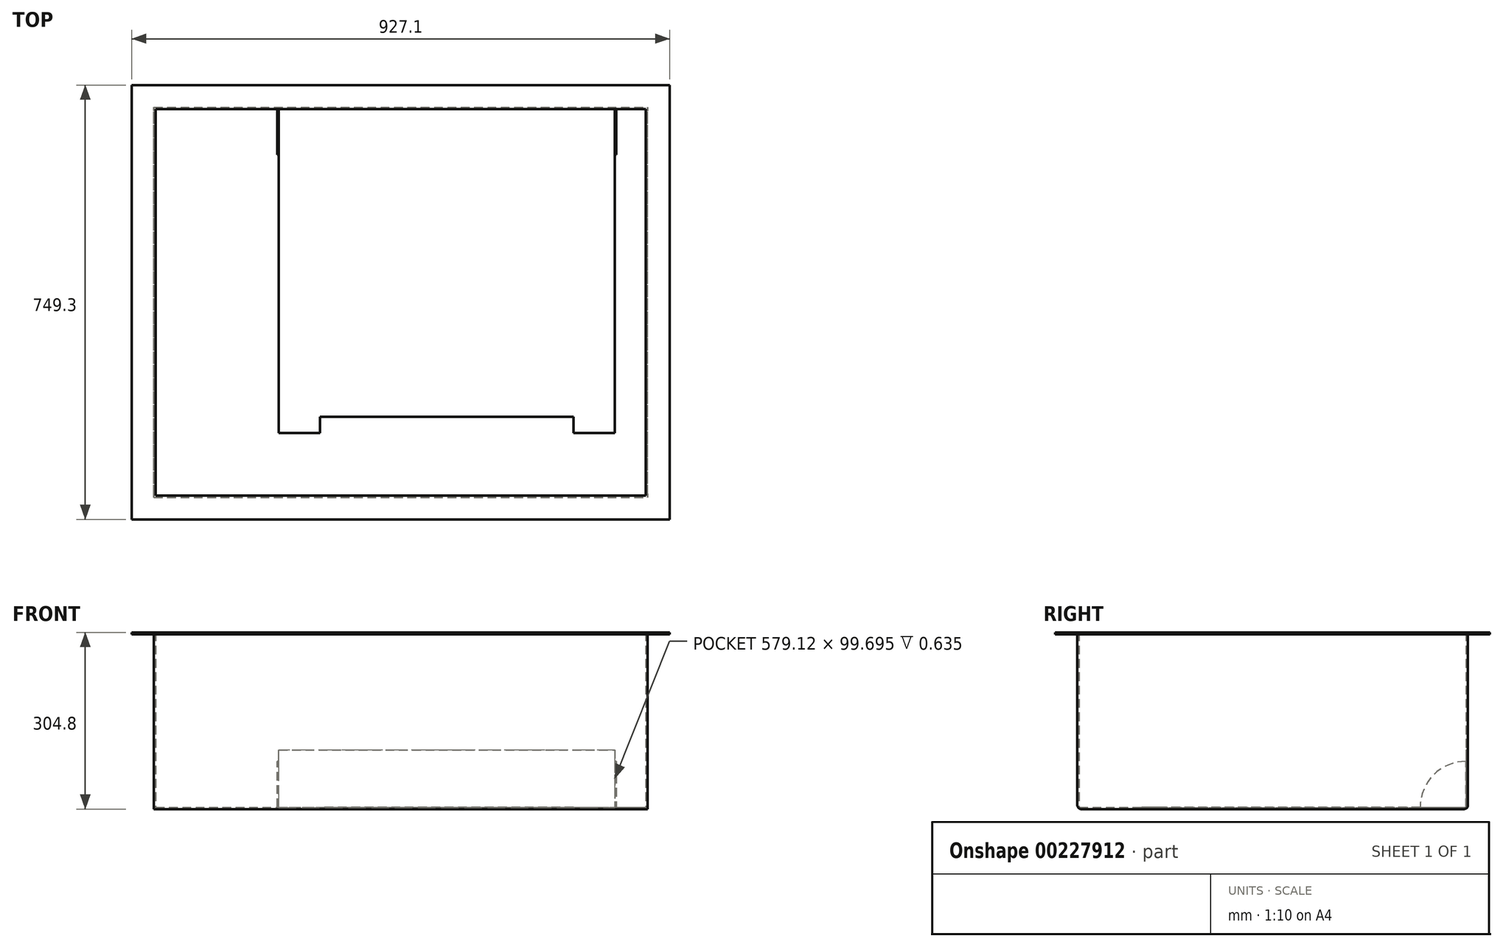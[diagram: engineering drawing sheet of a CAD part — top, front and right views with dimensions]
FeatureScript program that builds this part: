
annotation { "Feature Type Name" : "Feature", "Feature Type Description" : "" }
export const myFeature = defineFeature(function(context is Context, id is Id, definition is map)
    precondition{}
    {
        {
            var Q0;
            Q0=qCreatedBy(makeId("Top.planeOp"),FACE);
            var sketch = newSketch(context, id + "F0", { "sketchPlane" : qUnion([Q0])});
            skLineSegment(sketch, "E0.bottom", {"start": v(-425.45, -336.55) * mm, "end": v(425.45, -336.55) * mm});
            skLineSegment(sketch, "E0.top", {"start": v(-425.45, 336.55) * mm, "end": v(425.45, 336.55) * mm});
            skLineSegment(sketch, "E0.left", {"start": v(-425.45, -336.55) * mm, "end": v(-425.45, 336.55) * mm});
            skLineSegment(sketch, "E0.right", {"start": v(425.45, -336.55) * mm, "end": v(425.45, 336.55) * mm});
            skPoint(sketch, "E0.middle", {"position": v(0, 0) * mm});
            skSolve(sketch);
        }
        {
            var Q0;
            Q0=makeQuery(id+"F0.imprint","IMPRINT",FACE,{"disambiguationData":[TD([[makeQuery(id+"F0.imprint","IMPRINT",EDGE,{"derivedFrom":sQuery(id+"F0.wireOp",EDGE,"E0.bottom")}),1.0]])]});
            extrude(context, id + "F1", {"entities" : qUnion([Q0]), "depth" : 304.8 * mm});
        }
        {
            var Q0;
            Q0=makeQuery(id+"F1.opExtrude","CAP_FACE",FACE,{"disambiguationData":[OSD([sQuery(id+"F0.wireOp",EDGE,"E0.bottom"),sQuery(id+"F0.wireOp",EDGE,"E0.top"),sQuery(id+"F0.wireOp",EDGE,"E0.left"),sQuery(id+"F0.wireOp",EDGE,"E0.right")])],"isStart":false});
            shell(context, id + "F2", {"entities" : qUnion([Q0]), "thickness" : 3.17 * mm});
        }
        {
            var Q0;
            Q0=makeQuery(id+"F2.opShell","OFFSET_FACE",FACE,{"disambiguationData":[OSD([sQuery(id+"F0.wireOp",EDGE,"E0.top")])]});
            var sketch = newSketch(context, id + "F3", { "sketchPlane" : qUnion([Q0])});
            skLineSegment(sketch, "E1.0", {"start": v(371.48, 304.8) * mm, "end": v(371.48, 3.17) * mm});
            skLineSegment(sketch, "E2", {"start": v(371.48, 3.17) * mm, "end": v(-212.72, 3.17) * mm});
            skLineSegment(sketch, "E3", {"start": v(-212.72, 3.17) * mm, "end": v(-212.72, 104.78) * mm});
            skLineSegment(sketch, "E4", {"start": v(-212.72, 104.78) * mm, "end": v(371.48, 104.78) * mm});
            skSolve(sketch);
        }
        {
            var Q0;
            {var subQ0=sQuery(id+"F3.wireOp",EDGE,"E2");Q0=makeQuery(id+"F3.imprint","IMPRINT",FACE,{"disambiguationData":[TD([[makeQuery(id+"F3.imprint","IMPRINT",EDGE,{"derivedFrom":subQ0}),1.0]])]});}
            extrude(context, id + "F4", {"entities" : qUnion([Q0]), "operationType" : NewBodyOperationType.ADD, "depth" : 558.8 * mm});
        }
        {
            var Q0;
            Q0=makeQuery(id+"F4.opExtrude","CAP_FACE",FACE,{"disambiguationData":[OSD([sQuery(id+"F3.wireOp",EDGE,"E1.0"),sQuery(id+"F3.wireOp",EDGE,"E2"),sQuery(id+"F3.wireOp",EDGE,"E3"),sQuery(id+"F3.wireOp",EDGE,"E4")])],"isStart":false});
            var sketch = newSketch(context, id + "F5", { "sketchPlane" : qUnion([Q0])});
            skLineSegment(sketch, "E5.0", {"start": v(-136.52, 3.17) * mm, "end": v(-136.52, 104.78) * mm});
            skLineSegment(sketch, "E6.0", {"start": v(295.28, 104.78) * mm, "end": v(295.28, 3.17) * mm});
            skLineSegment(sketch, "E7.0", {"start": v(-212.72, 73.03) * mm, "end": v(371.48, 73.03) * mm});
            skSolve(sketch);
        }
        {
            var Q0;
            {var subQ0=sQuery(id+"F5.wireOp",EDGE,"E5.0");var subQ1=makeQuery(id+"F4.opExtrude","CAP_EDGE",EDGE,{"disambiguationData":[OSD([sQuery(id+"F3.wireOp",EDGE,"E2")])],"isStart":false});var subQ2=makeQuery(id+"F5.imprint","INTERSECT",VERTEX,{"derivedFrom":[subQ1,subQ0]});Q0=makeQuery(id+"F5.imprint","IMPRINT",FACE,{"disambiguationData":[TD([[makeQuery(id+"F5.imprint","IMPRINT",EDGE,{"disambiguationData":[TD([[subQ2,-1.0]])],"derivedFrom":subQ0}),-1.0]])]});}
            extrude(context, id + "F6", {"entities" : qUnion([Q0]), "operationType" : NewBodyOperationType.REMOVE, "oppositeDirection" : true, "depth" : 25.4 * mm});
        }
        {
            var Q0;
            Q0=makeQuery(id+"F4.opExtrude","CAP_FACE",FACE,{"disambiguationData":[OSD([sQuery(id+"F3.wireOp",EDGE,"E1.0"),sQuery(id+"F3.wireOp",EDGE,"E2"),sQuery(id+"F3.wireOp",EDGE,"E3"),sQuery(id+"F3.wireOp",EDGE,"E4")])],"isStart":false});
            shell(context, id + "F7", {"entities" : qUnion([Q0]), "thickness" : 2.54 * mm});
        }
        {
            var Q0;
            Q0=makeQuery(id+"F4.opExtrude","SWEPT_FACE",FACE,{"disambiguationData":[OSD([sQuery(id+"F3.wireOp",EDGE,"E4")])]});
            var sketch = newSketch(context, id + "F8", { "sketchPlane" : qUnion([Q0])});
            skLineSegment(sketch, "E8.0", {"start": v(-60.32, -225.43) * mm, "end": v(-60.32, 333.38) * mm, "construction": true});
            skLineSegment(sketch, "E9.0", {"start": v(219.08, -225.43) * mm, "end": v(219.08, 333.38) * mm, "construction": true});
            skLineSegment(sketch, "E10.0", {"start": v(-212.72, 269.88) * mm, "end": v(371.48, 269.88) * mm, "construction": true});
            skLineSegment(sketch, "E11.0", {"start": v(-212.72, -161.93) * mm, "end": v(371.48, -161.93) * mm, "construction": true});
            skCircle(sketch, "E12", {"center": v(-60.32, 269.88) * mm, "radius": 24.06 * mm, "construction": true});
            skCircle(sketch, "E13", {"center": v(219.08, 269.88) * mm, "radius": 28.85 * mm, "construction": true});
            skCircle(sketch, "E14", {"center": v(219.08, -161.93) * mm, "radius": 29.69 * mm, "construction": true});
            skCircle(sketch, "E15", {"center": v(-60.32, -161.93) * mm, "radius": 21.62 * mm, "construction": true});
            skCircle(sketch, "E16", {"center": v(-60.32, 269.88) * mm, "radius": 6.35 * mm});
            skCircle(sketch, "E17", {"center": v(219.08, 269.88) * mm, "radius": 6.35 * mm});
            skCircle(sketch, "E18", {"center": v(-60.32, -161.93) * mm, "radius": 6.35 * mm});
            skCircle(sketch, "E19", {"center": v(219.08, -161.93) * mm, "radius": 6.35 * mm});
            skSolve(sketch);
        }
        {
            var Q0;
            Q0=makeQuery(id+"F8.imprint","IMPRINT",FACE,{"disambiguationData":[TD([[makeQuery(id+"F8.imprint","IMPRINT",EDGE,{"derivedFrom":sQuery(id+"F8.wireOp",EDGE,"E17")}),1.0]])]});
            var Q1;
            Q1=makeQuery(id+"F8.imprint","IMPRINT",FACE,{"disambiguationData":[TD([[makeQuery(id+"F8.imprint","IMPRINT",EDGE,{"derivedFrom":sQuery(id+"F8.wireOp",EDGE,"E16")}),1.0]])]});
            var Q2;
            Q2=makeQuery(id+"F8.imprint","IMPRINT",FACE,{"disambiguationData":[TD([[makeQuery(id+"F8.imprint","IMPRINT",EDGE,{"derivedFrom":sQuery(id+"F8.wireOp",EDGE,"E18")}),1.0]])]});
            var Q3;
            Q3=makeQuery(id+"F8.imprint","IMPRINT",FACE,{"disambiguationData":[TD([[makeQuery(id+"F8.imprint","IMPRINT",EDGE,{"derivedFrom":sQuery(id+"F8.wireOp",EDGE,"E19")}),1.0]])]});
            extrude(context, id + "F9", {"entities" : qUnion([Q0, Q1, Q2, Q3]), "operationType" : NewBodyOperationType.REMOVE, "endBound" : BoundingType.UP_TO_NEXT, "oppositeDirection" : true, "depth" : 25.4 * mm});
        }
        {
            var Q0;
            Q0=makeQuery(id+"F1.opExtrude","CAP_FACE",FACE,{"disambiguationData":[OSD([sQuery(id+"F0.wireOp",EDGE,"E0.bottom"),sQuery(id+"F0.wireOp",EDGE,"E0.top"),sQuery(id+"F0.wireOp",EDGE,"E0.left"),sQuery(id+"F0.wireOp",EDGE,"E0.right")])],"isStart":false});
            var sketch = newSketch(context, id + "F10", { "sketchPlane" : qUnion([Q0])});
            skLineSegment(sketch, "E20.0", {"start": v(-463.55, 374.65) * mm, "end": v(463.55, 374.65) * mm});
            skLineSegment(sketch, "E21.0", {"start": v(-463.55, -374.65) * mm, "end": v(-463.55, 374.65) * mm});
            skLineSegment(sketch, "E22.0", {"start": v(463.55, -374.65) * mm, "end": v(463.55, 374.65) * mm});
            skLineSegment(sketch, "E23.0", {"start": v(-463.55, -374.65) * mm, "end": v(463.55, -374.65) * mm});
            skLineSegment(sketch, "E24.0", {"start": v(-425.45, -336.55) * mm, "end": v(-425.45, 336.55) * mm});
            skLineSegment(sketch, "E25.0", {"start": v(-425.45, -336.55) * mm, "end": v(425.45, -336.55) * mm});
            skLineSegment(sketch, "E26.0", {"start": v(-425.45, 336.55) * mm, "end": v(425.45, 336.55) * mm});
            skLineSegment(sketch, "E27.0", {"start": v(425.45, -336.55) * mm, "end": v(425.45, 336.55) * mm});
            skSolve(sketch);
        }
        {
            var Q0;
            Q0=makeQuery(id+"F10.imprint","IMPRINT",FACE,{"disambiguationData":[TD([[makeQuery(id+"F10.imprint","IMPRINT",EDGE,{"derivedFrom":sQuery(id+"F10.wireOp",EDGE,"E20.0")}),-1.0]])]});
            extrude(context, id + "F11", {"entities" : qUnion([Q0]), "operationType" : NewBodyOperationType.ADD, "oppositeDirection" : true, "depth" : 3.17 * mm});
        }
        {
            var Q0;
            Q0=makeQuery(id+"F1.opExtrude","CAP_EDGE",EDGE,{"disambiguationData":[OSD([sQuery(id+"F0.wireOp",EDGE,"E0.bottom")])],"isStart":true});
            fillet(context, id + "F12", {"entities" : qUnion([Q0]), "radius" : 6.35 * mm, "tangentPropagation" : true, "allowEdgeOverflow" : false});
        }
        {
            var Q0;
            Q0=makeQuery(id+"F1.opExtrude","CAP_EDGE",EDGE,{"disambiguationData":[OSD([sQuery(id+"F0.wireOp",EDGE,"E0.top")])],"isStart":true});
            fillet(context, id + "F13", {"entities" : qUnion([Q0]), "radius" : 6.35 * mm, "tangentPropagation" : true, "allowEdgeOverflow" : false});
        }
        {
            var Q0;
            Q0=makeQuery(id+"F4.opExtrude","SWEPT_FACE",FACE,{"disambiguationData":[OSD([sQuery(id+"F3.wireOp",EDGE,"E3")])]});
            var sketch = newSketch(context, id + "F14", { "sketchPlane" : qUnion([Q0])});
            skArc(sketch, "E28", {"start": v(-333.38, 82.32) * mm, "mid": v(-277.4, 59.14) * mm, "end": v(-254.23, 3.17) * mm});
            skSolve(sketch);
        }
        {
            var Q0;
            {var subQ0=sQuery(id+"F14.wireOp",EDGE,"E28");Q0=makeQuery(id+"F14.imprint","IMPRINT",FACE,{"disambiguationData":[TD([[makeQuery(id+"F14.imprint","IMPRINT",EDGE,{"derivedFrom":subQ0}),-1.0]])]});}
            var Q1;
            Q1=makeQuery(id+"F4.opExtrude","SWEPT_FACE",FACE,{"disambiguationData":[OSD([sQuery(id+"F3.wireOp",EDGE,"E1.0")])]});
            extrude(context, id + "F15", {"entities" : qUnion([Q0]), "operationType" : NewBodyOperationType.REMOVE, "endBound" : BoundingType.UP_TO_SURFACE, "oppositeDirection" : true, "endBoundEntityFace" : qUnion([Q1]), "depth" : 25.4 * mm});
        }
    });
